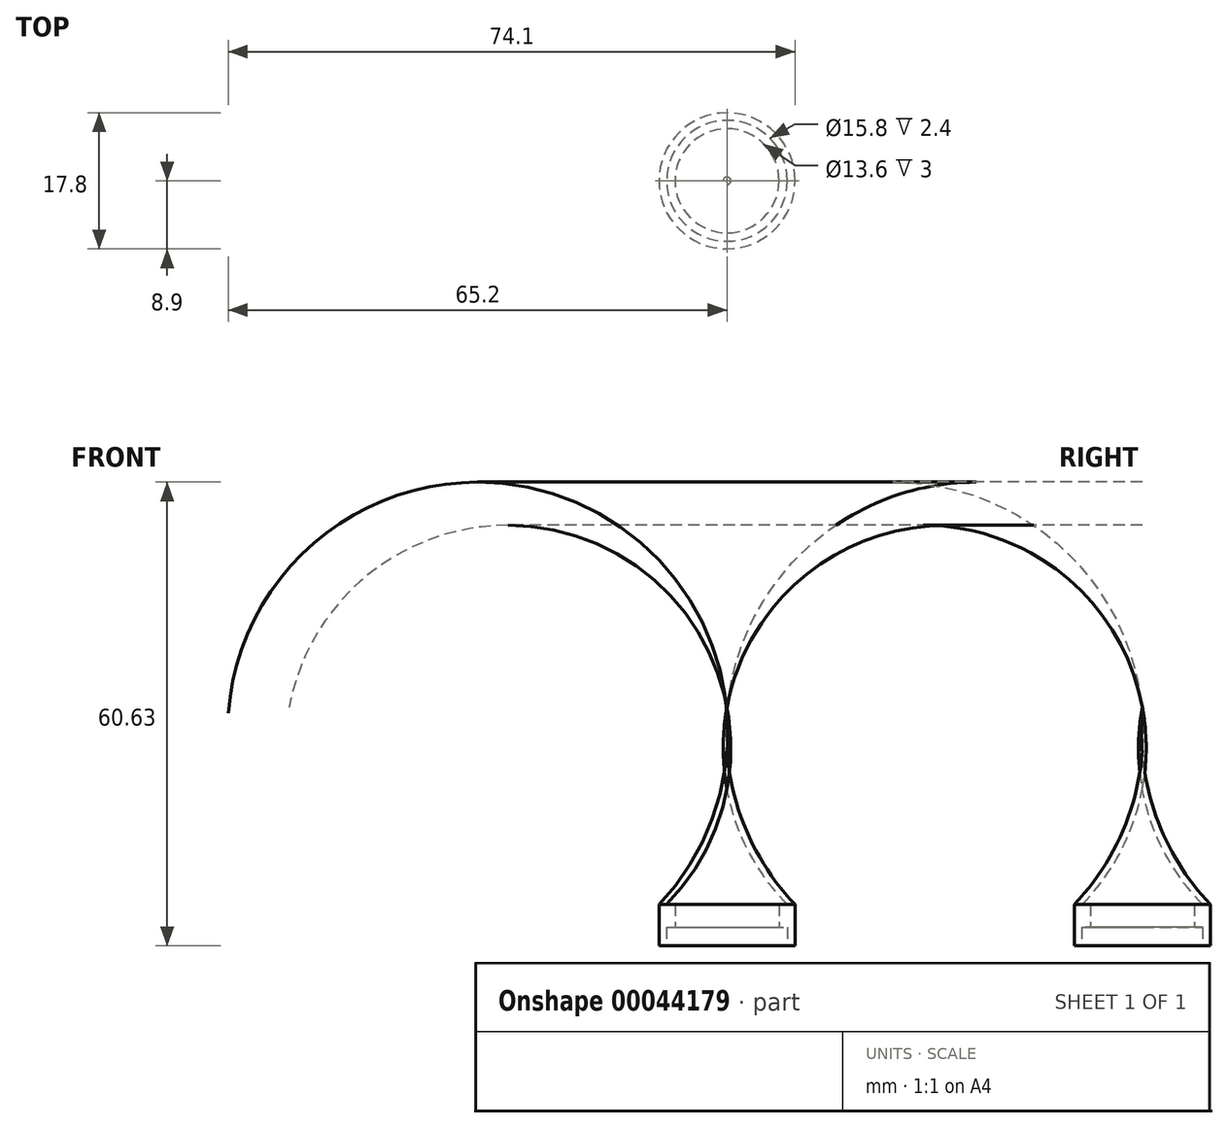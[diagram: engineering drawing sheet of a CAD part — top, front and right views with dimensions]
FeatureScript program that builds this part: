
annotation { "Feature Type Name" : "Feature", "Feature Type Description" : "" }
export const myFeature = defineFeature(function(context is Context, id is Id, definition is map)
    precondition{}
    {
        {
            var Q0;
            Q0=qCreatedBy(makeId("Front.planeOp"),FACE);
            var sketch = newSketch(context, id + "F0", { "sketchPlane" : qUnion([Q0])});
            skLineSegment(sketch, "E0", {"start": v(-17.52, 0) * mm, "end": v(42.68, 0) * mm, "construction": true});
            skLineSegment(sketch, "E1", {"start": v(0, 0) * mm, "end": v(0, 7.9) * mm, "construction": true});
            skLineSegment(sketch, "E2", {"start": v(0, 7.9) * mm, "end": v(2.4, 7.9) * mm});
            skLineSegment(sketch, "E3", {"start": v(2.4, 6.8) * mm, "end": v(2.4, 7.9) * mm});
            skLineSegment(sketch, "E4", {"start": v(2.4, 6.8) * mm, "end": v(5.4, 6.8) * mm});
            skLineSegment(sketch, "E5", {"start": v(0, 7.9) * mm, "end": v(0, 8.9) * mm});
            skLineSegment(sketch, "E6", {"start": v(5.4, 6.8) * mm, "end": v(5.4, 7.9) * mm});
            skLineSegment(sketch, "E7", {"start": v(0, 8.9) * mm, "end": v(5.4, 8.9) * mm});
            skLineSegment(sketch, "E8", {"start": v(2.4, 7.9) * mm, "end": v(5.4, 7.9) * mm, "construction": true});
            skLineSegment(sketch, "E9", {"start": v(20.5, 0) * mm, "end": v(25.4, 0) * mm});
            skArc(sketch, "E10", {"start": v(5.4, 8.9) * mm, "mid": v(14.63, 2.73) * mm, "end": v(25.4, 0) * mm});
            skArc(sketch, "E11", {"start": v(5.4, 7.9) * mm, "mid": v(12.36, 2.82) * mm, "end": v(20.5, 0) * mm});
            skLineSegment(sketch, "E12", {"start": v(5.4, 8.9) * mm, "end": v(5.4, 28.15) * mm, "construction": true});
            skSolve(sketch);
        }
        {
            var Q0;
            Q0=makeQuery(id+"F0.imprint","IMPRINT",FACE,{"disambiguationData":[TD([[makeQuery(id+"F0.imprint","IMPRINT",EDGE,{"derivedFrom":sQuery(id+"F0.wireOp",EDGE,"E2")}),1.0]])]});
            var Q1;
            Q1=sQuery(id+"F0.wireOp",EDGE,"E0");
            revolve(context, id + "F1", {"entities" : qUnion([Q0]), "axis" : qUnion([Q1]), "revolveType" : RevolveType.FULL});
        }
        {
            var Q0;
            Q0=qCreatedBy(makeId("Front.planeOp"),FACE);
            var sketch = newSketch(context, id + "F2", { "sketchPlane" : qUnion([Q0])});
            skCircle(sketch, "E13", {"center": v(0, 0) * mm, "radius": 5.79 * mm});
            skSolve(sketch);
        }
        {
            var Q0;
            Q0=makeQuery(id+"F1.opRevolve","SWEPT_BODY",BODY,{"disambiguationData":[OSD([sQuery(id+"F0.wireOp",EDGE,"E2"),sQuery(id+"F0.wireOp",EDGE,"E3"),sQuery(id+"F0.wireOp",EDGE,"E4"),sQuery(id+"F0.wireOp",EDGE,"E5"),sQuery(id+"F0.wireOp",EDGE,"E6"),sQuery(id+"F0.wireOp",EDGE,"E7"),sQuery(id+"F0.wireOp",EDGE,"E9"),sQuery(id+"F0.wireOp",EDGE,"E10"),sQuery(id+"F0.wireOp",EDGE,"E11")])]});
            var Q1;
            Q1=sQuery(id+"F2.wireOp",EDGE,"E13");
            transform(context, id + "F3", {"entities" : qUnion([Q0]), "transformType" : TransformType.ROTATION, "transformAxis" : qUnion([Q1]), "angle" : 90 * degree, "makeCopy" : false});
        }
    });
